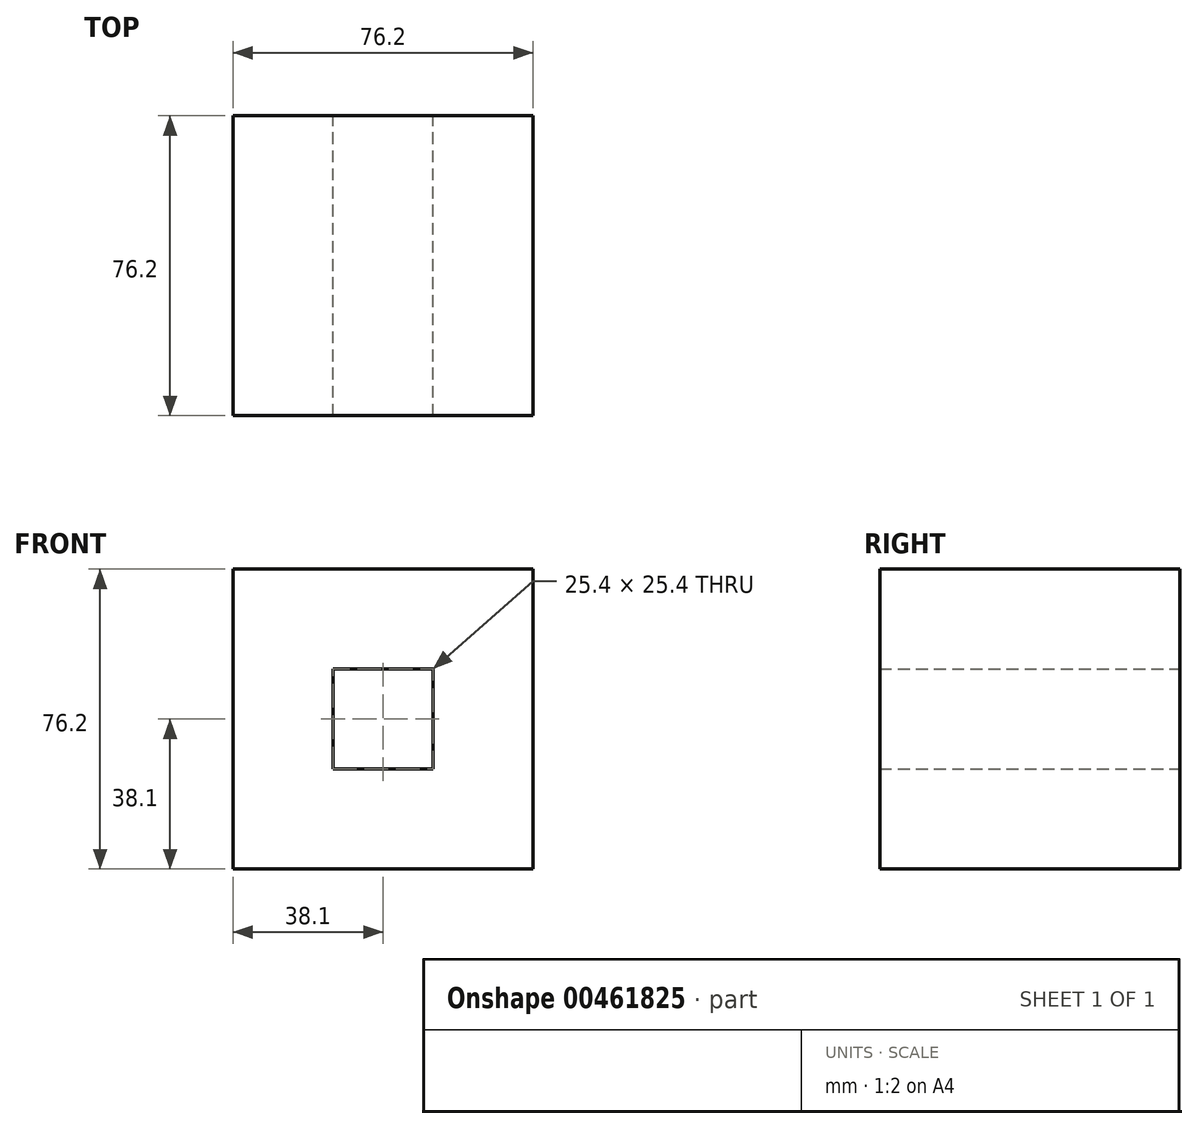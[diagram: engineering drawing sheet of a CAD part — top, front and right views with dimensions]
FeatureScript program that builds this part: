
annotation { "Feature Type Name" : "Feature", "Feature Type Description" : "" }
export const myFeature = defineFeature(function(context is Context, id is Id, definition is map)
    precondition{}
    {
        {
            var Q0;
            Q0=qCreatedBy(makeId("Front.planeOp"),FACE);
            var sketch = newSketch(context, id + "F0", { "sketchPlane" : qUnion([Q0])});
            skLineSegment(sketch, "E0.bottom", {"start": v(38.1, 38.1) * mm, "end": v(-38.1, 38.1) * mm});
            skLineSegment(sketch, "E0.top", {"start": v(38.1, -38.1) * mm, "end": v(-38.1, -38.1) * mm});
            skLineSegment(sketch, "E0.left", {"start": v(38.1, 38.1) * mm, "end": v(38.1, -38.1) * mm});
            skLineSegment(sketch, "E0.right", {"start": v(-38.1, 38.1) * mm, "end": v(-38.1, -38.1) * mm});
            skPoint(sketch, "E0.middle", {"position": v(0, 0) * mm});
            skSolve(sketch);
        }
        {
            var Q0;
            Q0=makeQuery(id+"F0.imprint","IMPRINT",FACE,{"disambiguationData":[TD([[makeQuery(id+"F0.imprint","IMPRINT",EDGE,{"derivedFrom":sQuery(id+"F0.wireOp",EDGE,"E0.bottom")}),1.0]])]});
            extrude(context, id + "F1", {"entities" : qUnion([Q0]), "depth" : 76.2 * mm});
        }
        {
            var Q0;
            Q0=qCreatedBy(makeId("Front.planeOp"),FACE);
            var sketch = newSketch(context, id + "F2", { "sketchPlane" : qUnion([Q0])});
            skLineSegment(sketch, "E1.bottom", {"start": v(12.7, -12.7) * mm, "end": v(-12.7, -12.7) * mm});
            skLineSegment(sketch, "E1.top", {"start": v(12.7, 12.7) * mm, "end": v(-12.7, 12.7) * mm});
            skLineSegment(sketch, "E1.left", {"start": v(12.7, -12.7) * mm, "end": v(12.7, 12.7) * mm});
            skLineSegment(sketch, "E1.right", {"start": v(-12.7, -12.7) * mm, "end": v(-12.7, 12.7) * mm});
            skPoint(sketch, "E1.middle", {"position": v(0, 0) * mm});
            skSolve(sketch);
        }
        {
            var Q0;
            Q0 = qSketchRegion(id + "F2", true);
            extrude(context, id + "F3", {"entities" : qUnion([Q0]), "operationType" : NewBodyOperationType.REMOVE, "endBound" : BoundingType.THROUGH_ALL, "depth" : 25.4 * mm});
        }
    });
